# Revit family: 2103A_Dimming_WASP
name_source: partatom
category: Communication Devices
revit_build: Autodesk Revit 2014 (Build: 20130308_1515(x64)
units: mm (PartAtom-declared; Revit-internal decimal feet)

## types (1)
- 2103A_Dimming_WASP
    Assembly Code = D5090
    Certifications = Conforms to UL STD 508, UL STD 244A
LWO version conforms to IP65
    Coverage = Indoor-360° degree (masking kit included)
    Default Elevation = 48 "
    Description = The WASP2 Occupancy Sensor is an Indoor Sensor, specifically
designed for ON/OFF control of high bay fixtures in warehouse,
distribution centers and similar facilities.
    Features = Digital Passive Infrared (PIR) sensor 
Mounting height is 45 ft indoor only 
Single output
End Mount installation 
Daylight sensor for daylight harvesting applications
UL and cUL listed 
Five-year limited warranty 
Kit includes WASP2 Occupancy Sensor, Lens, Adaptor and Masking Kit
    Housing Material = Paint - Hubbell - Matte White
    Manufacturer = Hubbell Control Solutions
    Model = WASP™2Occupancy Sensor Kit
    Power Requirements = Line Voltage sensors: 120/277/347VAC, 60 Hz
    Product Documentation Link = https://hubbellcdn.com
    Product Page URL = https://www.hubbell.com
    Sensing Element = Glass - Hubbell - White
    Type Comments = Occupancy Sensors and Controllers
    URL = https://www.hubbell.com
    Warranty = 5-Years Warranty
    Width = 4 "

## geometry (parser evidence)
native form markers: Sweep x1
no freeform markers — native parametric forms only
